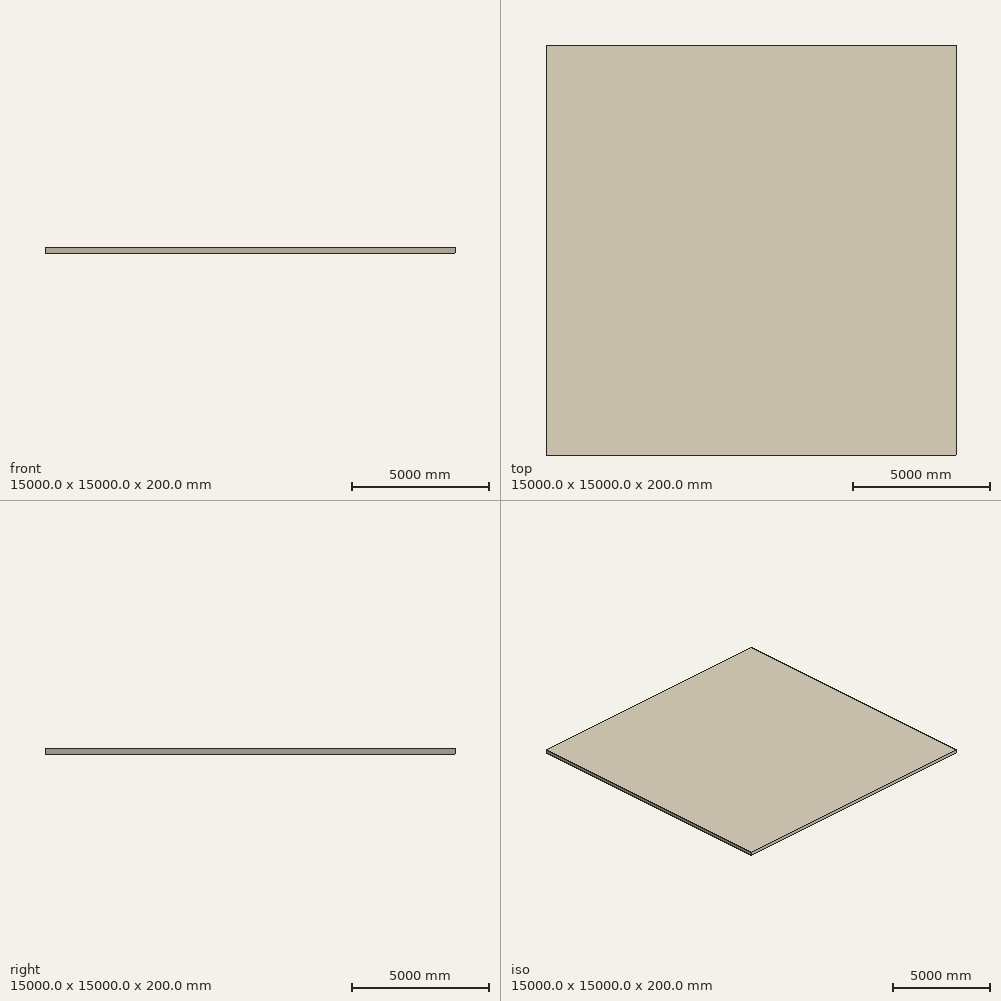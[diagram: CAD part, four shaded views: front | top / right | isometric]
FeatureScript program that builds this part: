
annotation { "Feature Type Name" : "Feature", "Feature Type Description" : "" }
export const myFeature = defineFeature(function(context is Context, id is Id, definition is map)
    precondition{}
    {
        {
            var Q0;
            Q0=qCreatedBy(makeId("Top.planeOp"),FACE);
            var sketch = newSketch(context, id + "F0", { "sketchPlane" : qUnion([Q0])});
            skLineSegment(sketch, "E0.bottom", {"start": v(5377.74, 8440.5) * mm, "end": v(-9622.26, 8440.5) * mm});
            skLineSegment(sketch, "E0.top", {"start": v(5377.74, -6559.5) * mm, "end": v(-9622.26, -6559.5) * mm});
            skLineSegment(sketch, "E0.left", {"start": v(5377.74, 8440.5) * mm, "end": v(5377.74, -6559.5) * mm});
            skLineSegment(sketch, "E0.right", {"start": v(-9622.26, 8440.5) * mm, "end": v(-9622.26, -6559.5) * mm});
            skSolve(sketch);
        }
        {
            var Q0;
            Q0=makeQuery(id+"F0.imprint","IMPRINT",FACE,{"disambiguationData":[TD([[makeQuery(id+"F0.imprint","IMPRINT",EDGE,{"derivedFrom":sQuery(id+"F0.wireOp",EDGE,"E0.bottom")}),1.0]])]});
            extrude(context, id + "F1", {"entities" : qUnion([Q0]), "oppositeDirection" : true, "depth" : 200 * mm});
        }
    });
